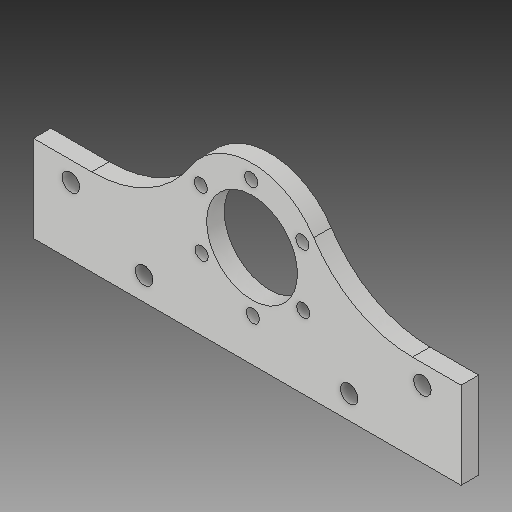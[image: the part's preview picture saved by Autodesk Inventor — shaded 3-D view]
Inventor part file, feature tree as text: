
AUTODESK INVENTOR PART (.ipt)
format: ipt  version: 2018 (Build 220112000, 112)  size: 145,408 bytes
history: native  units: mm
features: reference x13, extrude x4, sketch x4, fillet x1
ambient origin geometry x8: Origin, YZ Plane, XZ Plane, XY Plane, X Axis, Y Axis, Z Axis, Center Point
bodies: Solid1 (feature_tree)
feature tree (22):
  extrude  "Extrusion1"  Depth=6.0mm TaperAngle=0.0deg
  extrude  "Extrusion2"  Depth=6.0mm
  extrude  "Extrusion3"  Depth=60.0mm
  extrude  "Extrusion4"  Depth=40.0mm
  fillet  "Fillet2"  Radius=35.0mm
  sketch  "Sketch1"  dims[d0=34.0mm d1=6.0mm d2=0.0mm]
  reference  "Reference1"
  reference  "Reference2"
  reference  "Reference3"
  sketch  "Sketch2"  dims[d3=6.0mm d4=6.0mm]
  sketch  "Sketch3"  dims[d6=15.0mm d7=60.0mm]
  reference  "Reference5"
  reference  "Reference6"
  reference  "Reference7"
  reference  "Reference8"
  reference  "Reference9"
  reference  "Reference10"
  reference  "Reference11"
  sketch  "Sketch5"  dims[d8=6.0mm d9=0.0mm d10=8.0mm d11=35.0mm d12=6.0mm d13=0.0mm d14=0.5mm d16=6.0mm d17=0.0mm d18=40.0mm]
  reference  "Reference12"
  reference  "Reference13"
  reference  "Reference14"
